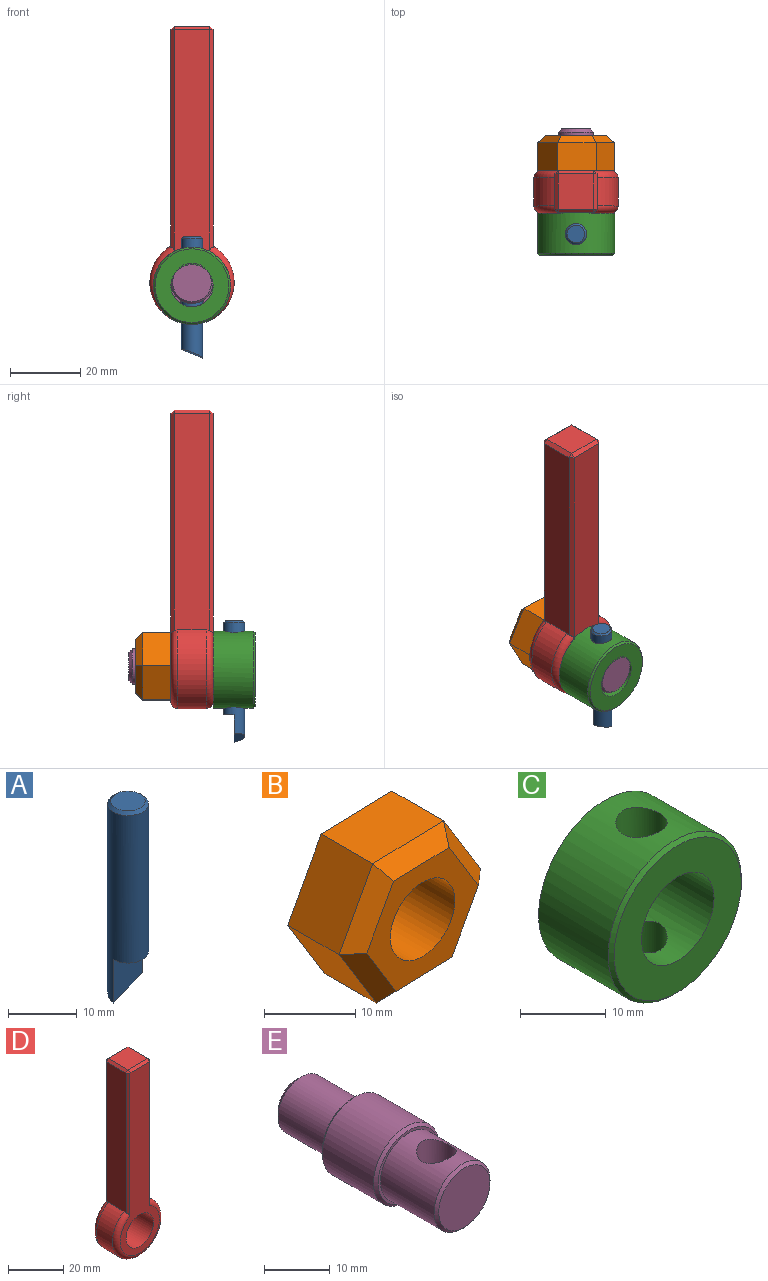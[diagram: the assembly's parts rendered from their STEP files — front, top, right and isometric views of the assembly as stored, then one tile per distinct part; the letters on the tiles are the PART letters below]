
ASSEMBLY  parts=5 mates=4
PART A: 6 faces, bbox 6x6x34.5 mm
  f0: cylinder r=3mm len=34.02mm, axis (0,0,-1), area 554.4mm2, adj f2,f3,f4,f5
  f1: plane 5x5mm, normal (0,0,1), area 19.6mm2, adj f2
  f2: cone r=2.5mm half-angle=45deg, axis (0,0,-1), area 12.2mm2, adj f0,f1
  f3: plane 6x3mm, normal (0,0,-1), area 14.1mm2, adj f0,f4
  f4: plane 7.74x6mm, normal (0,-1,0), area 39.2mm2, adj f0,f3,f5
  f5: plane 6x3mm, normal (0.37,0.14,-0.92), area 15.4mm2, adj f0,f4
PART B: 15 faces, bbox 21.9x10x19.3 mm
  f0: plane 9.35x8mm, normal (-0.85,0,-0.52), area 87.8mm2, adj f1,f6,f8,f10
  f1: plane 10.97x8mm, normal (0.03,0,-1), area 87.8mm2, adj f0,f2,f8,f9
  f2: plane 9.65x8mm, normal (0.88,0,-0.48), area 87.8mm2, adj f1,f3,f8,f11
  f3: plane 9.35x8mm, normal (0.85,0,0.52), area 87.8mm2, adj f2,f4,f8,f13
  f4: plane 10.97x8mm, normal (-0.03,0,1), area 87.8mm2, adj f3,f6,f8,f14
  f5: cylinder r=5mm len=10mm, axis (0,1,0), area 314.2mm2, adj f7,f8
  f6: plane 9.65x8mm, normal (-0.88,0,0.48), area 87.8mm2, adj f0,f4,f8,f12
  f7: plane 17.32x15.24mm, normal (0,-1,0), area 116.5mm2, adj f5,f9,f10,f11,f12,f13,f14
  f8: plane 21.94x19.3mm, normal (0,1,0), area 234.3mm2, adj f0,f1,f2,f3,f4,f5,f6
  f9: plane 10.97x2.27mm, normal (0.02,-0.71,-0.71), area 27.8mm2, adj f1,f7,f10,f11
  f10: plane 9.41x6.84mm, normal (-0.6,-0.71,-0.37), area 27.8mm2, adj f0,f7,f9,f12
  f11: plane 9.65x6.44mm, normal (0.62,-0.71,-0.34), area 27.8mm2, adj f2,f7,f9,f13
  f12: plane 9.65x6.44mm, normal (-0.62,-0.71,0.34), area 27.8mm2, adj f6,f7,f10,f14
  f13: plane 9.41x6.84mm, normal (0.6,-0.71,0.37), area 27.8mm2, adj f3,f7,f11,f14
  f14: plane 10.97x2.27mm, normal (-0.02,-0.71,0.71), area 27.8mm2, adj f4,f7,f12,f13
PART C: 7 faces, bbox 22x12x22 mm
  f0: cylinder r=6mm len=12mm, axis (0,1,0), area 393.8mm2, adj f2,f3,f5,f6
  f1: cylinder r=11mm len=22mm, axis (0,1,0), area 737.7mm2, adj f3,f4,f5,f6
  f2: plane 21x21mm, normal (0,-1,0), area 233.3mm2, adj f0,f4
  f3: plane 22x22mm, normal (0,1,0), area 267mm2, adj f0,f1
  f4: cone r=10.5mm half-angle=45deg, axis (0,1,0), area 47.8mm2, adj f1,f2
  f5: cylinder r=3mm len=6mm, axis (0,0,-1), area 97.8mm2, adj f0,f1
  f6: cylinder r=3mm len=6mm, axis (0,0,-1), area 97.8mm2, adj f0,f1
PART D: 21 faces, bbox 26x12x86 mm
  f0: plane 61.92x10mm, normal (-1,0,0), area 616.3mm2, adj f5,f7,f8,f14,f18,f20
  f1: plane 61.92x10mm, normal (1,0,0), area 616.3mm2, adj f5,f7,f8,f9,f11,f12
  f2: plane 82x20mm, normal (0,-1,0), area 784.6mm2, adj f6,f8,f9,f13,f14
  f3: plane 82x20mm, normal (0,1,0), area 784.6mm2, adj f6,f7,f11,f17,f20
  f4: plane 10x10mm, normal (0,0,1), area 100mm2, adj f12,f13,f17,f18
  f5: cylinder r=12mm len=24mm, axis (0,1,0), area 502.7mm2, adj f0,f1,f7,f8
  f6: cylinder r=7mm len=14mm, axis (0,1,0), area 527.8mm2, adj f2,f3
  f7: torus R=10mm, axis (0,1,0), area 186mm2, adj f0,f1,f3,f5,f11,f20
  f8: torus R=10mm, axis (0,1,0), area 186mm2, adj f0,f1,f2,f5,f9,f14
  f9: plane 63.34x1mm, normal (0.71,-0.71,0), area 88mm2, adj f1,f2,f8,f10
  f10: plane 1x1mm, normal (0.58,-0.58,0.58), area 0.9mm2, adj f9,f12,f13
  f11: plane 63.34x1mm, normal (0.71,0.71,0), area 88mm2, adj f1,f3,f7,f15
  f12: plane 10x1mm, normal (0.71,0,0.71), area 14.1mm2, adj f1,f4,f10,f15
  f13: plane 10x1mm, normal (0,-0.71,0.71), area 14.1mm2, adj f2,f4,f10,f16
  f14: plane 63.34x1mm, normal (-0.71,-0.71,0), area 88mm2, adj f0,f2,f8,f16
  f15: plane 1x1mm, normal (0.58,0.58,0.58), area 0.9mm2, adj f11,f12,f17
  f16: plane 1x1mm, normal (-0.58,-0.58,0.58), area 0.9mm2, adj f13,f14,f18
  f17: plane 10x1mm, normal (0,0.71,0.71), area 14.1mm2, adj f3,f4,f15,f19
  f18: plane 10x1mm, normal (-0.71,0,0.71), area 14.1mm2, adj f0,f4,f16,f19
  f19: plane 1x1mm, normal (-0.58,0.58,0.58), area 0.9mm2, adj f17,f18,f20
  f20: plane 63.34x1mm, normal (-0.71,0.71,0), area 88mm2, adj f0,f3,f7,f19
PART E: 12 faces, bbox 14x36x14 mm
  f0: cylinder r=7mm len=14mm, axis (0,1,0), area 483.8mm2, adj f8,f9
  f1: plane 13x13mm, normal (0,-1,0), area 19.6mm2, adj f3,f9
  f2: plane 13x13mm, normal (0,1,0), area 54.2mm2, adj f5,f8
  f3: cylinder r=6mm len=12mm, axis (0,1,0), area 375.1mm2, adj f1,f10,f11
  f4: plane 11x11mm, normal (0,-1,0), area 95mm2, adj f10
  f5: cylinder r=5mm len=11mm, axis (0,1,0), area 345.6mm2, adj f2,f7
  f6: plane 8x8mm, normal (0,1,0), area 50.3mm2, adj f7
  f7: cone r=5mm half-angle=45deg, axis (0,-1,0), area 40mm2, adj f5,f6
  f8: cone r=7mm half-angle=45deg, axis (0,-1,0), area 30mm2, adj f0,f2
  f9: cone r=6.5mm half-angle=45deg, axis (0,1,0), area 30mm2, adj f0,f1
  f10: cone r=5.5mm half-angle=45deg, axis (0,1,0), area 25.5mm2, adj f3,f4
  f11: cylinder r=3mm len=12mm, axis (0,0,1), area 211.3mm2, adj f3
PLACE A rot(axis=(0,0,1),180deg) t=(-23.02,-9.22,-33.8)mm
PLACE B rot(axis=(-1,0,0),180deg) t=(-23.02,8.78,-11.82)mm
PLACE C t=(-23.02,-3.22,-12.75)mm
PLACE D rot(axis=(1,0,0),0deg) t=(-23.02,2.78,-3.82)mm
PLACE E t=(-23.02,8.78,-11.82)mm
MATE revolute B.f5 <-> E.f0  axis (0,-1,0) through (-23.02,8.78,-11.82)mm
MATE revolute E.f0 <-> D.f5  axis (0,1,0) through (-23.02,8.78,-11.82)mm
MATE fastened C.f5 <-> E.f11  axis (0,0,-1) through (-23.02,-9.22,-17.9)mm
MATE slider A.f0 <-> E.f11  axis (0,0,1) through (-23.02,-9.22,1.2)mm
